# Revit family: Absperrventil 4125 AD
name_source: partatom
category: Rohrzubehör
units: mm (PartAtom-declared; Revit-internal decimal feet)

## family parameters
Arbeitsebenenbasiert = Nein
Beim Laden mit Abzugskörper schneiden = Nein
Bemaßung runder Anschluss = Durchmesser verwenden
Gemeinsam genutzt = Nein
Immer vertikal = Ja
OmniClass-Nummer = 23.65.55.14
OmniClass-Titel = Valves for Liquid Services
Teiletyp = Unterbricht

## types (1)
- Absperrventil 4125 AD
    Anwendungsgebiet = Zuverlässiges Absperren von Leitungen in Heiz- und Kühlanalgen.
    Ausführung = STRÖMAX-D-Absperrventile in Schrägsitzform, gelbe Ausführung, Muffe x Muffe,
mit langen Gewindemuffen, mit  2 Anbohrungen für Entleerungsarmaturen,
1 Verschlussschraube 1 0273 0x ist aufgeschraubt, nichtsteigender Spindel,
Spindelabdichtung durch elastischen Doppel-O-Ring.
Entleerungsventile sind separat zu bestellen.
    Dichtungen = EPDM
    Gehäuse = entzinkungsbeständiges Gussmessing CC752S
    Handrad = Polyamide
    Hersteller = HERZ Armaturen Ges.m.b.H.
    Kegel = entzinkungsbeständiges Messing CW602N
    L03 = 15 mm
    Max.Betriebsdruck = 2000000.0 Pa
    Max.Betriebstemperatur = 110 °C
    Max.Differenzdruck bei geschlossenen Sitz = 1000000.0 Pa
    Medium = Heizungswasser nach ÖNORM H5195 oder VDI- Richtlinie 2035.
Die Verwendung von Ethylen- oder Propyleneglykol in einem Mischungsverhältnis 25- 50% ist zulässig.
EPDM-Dichtungen können durch Mineralöle und Schmiermittel beeinflusst werden, was zum Versagen der EPDM-Dichtungen führen kann.
    Oberteil = entzinkungsbeständiges Messing CW602N
    R03 = 9.5 mm  [stored 0.031168 ft]
    R100 = 1 mm  [stored 0.00328084 ft]
    S03 = 60 mm
    SCRNCODE = 05;07;02
    SCRNSEQ = ARM;ARM_TYP="ABSV";2
    SW01 = 60.00°
    Spindel = Messing CW617N
    URL = www.herz-armaturen.at
    W01 = 45.00°

note: [stored X ft] marks values corroborated as IEEE doubles in the binary element streams (Revit-internal decimal feet)
